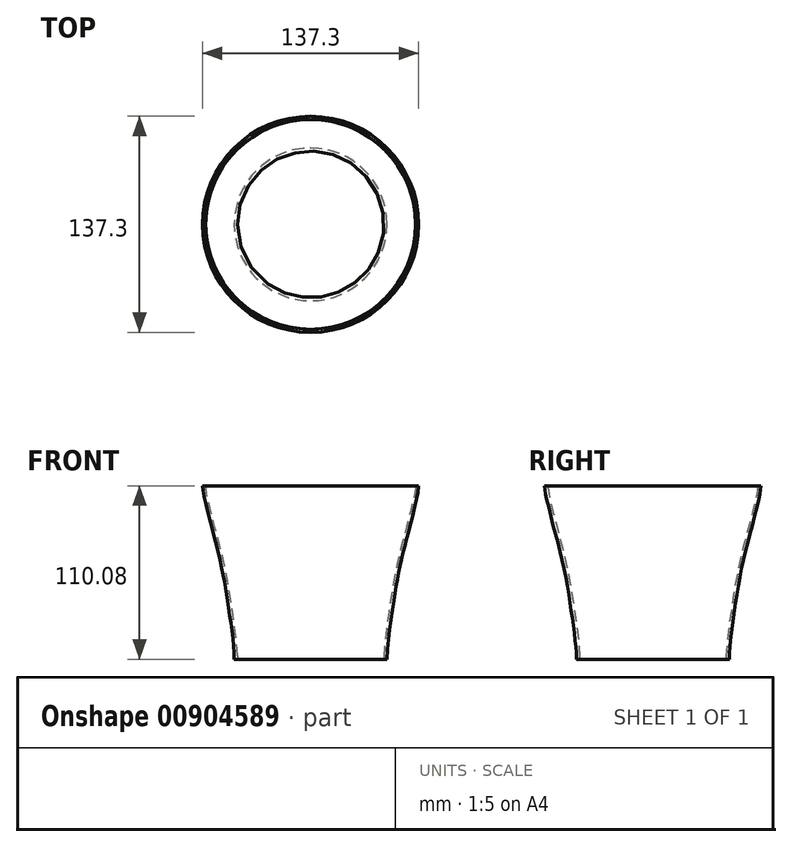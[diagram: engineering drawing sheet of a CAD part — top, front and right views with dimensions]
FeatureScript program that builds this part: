
annotation { "Feature Type Name" : "Feature", "Feature Type Description" : "" }
export const myFeature = defineFeature(function(context is Context, id is Id, definition is map)
    precondition{}
    {
        {
            var Q0;
            Q0=qCreatedBy(makeId("Front.planeOp"),FACE);
            var sketch = newSketch(context, id + "F0", { "sketchPlane" : qUnion([Q0])});
            skFitSpline(sketch, "E0", {"points": [v(-48.52, 0) * mm, v(-52.42, 34.55) * mm, v(-58.26, 65.75) * mm, v(-68.65, 110.08) * mm], "startDerivative": vector(0, 87.27) * mm, "endDerivative": vector(0, 50.37) * mm});
            skFitSpline(sketch, "E1.0", {"points": [v(-46.52, 0) * mm, v(-46.52, 1.88) * mm, v(-46.7, 5.96) * mm, v(-47.33, 12.74) * mm, v(-48.23, 19.89) * mm, v(-49.08, 25.86) * mm, v(-49.78, 30.48) * mm, v(-50.29, 33.83) * mm, v(-50.77, 37) * mm, v(-51.39, 41.06) * mm, v(-52.15, 45.92) * mm, v(-53.17, 51.81) * mm, v(-54.22, 57.08) * mm, v(-55.25, 61.72) * mm, v(-56.12, 65.44) * mm, v(-57.12, 69.48) * mm, v(-58.57, 75.18) * mm, v(-60.54, 82.68) * mm, v(-62.87, 91.6) * mm, v(-64.55, 98.37) * mm, v(-65.6, 103.04) * mm, v(-66.19, 106.07) * mm, v(-66.5, 108.11) * mm, v(-66.63, 109.38) * mm, v(-66.65, 109.88) * mm, v(-66.65, 110.08) * mm]});
            skLineSegment(sketch, "E2", {"start": v(-48.52, 0) * mm, "end": v(-46.52, 0) * mm});
            skLineSegment(sketch, "E3", {"start": v(-68.65, 110.08) * mm, "end": v(-66.65, 110.08) * mm});
            skLineSegment(sketch, "E4.bottom", {"start": v(-48.52, 0) * mm, "end": v(0, 0) * mm});
            skLineSegment(sketch, "E4.top", {"start": v(-46.55, 2) * mm, "end": v(0, 2) * mm});
            skLineSegment(sketch, "E4.left", {"start": v(-48.52, 0) * mm, "end": v(-48.52, 2) * mm});
            skLineSegment(sketch, "E4.right", {"start": v(0, 0) * mm, "end": v(0, 2) * mm});
            skSolve(sketch);
        }
        {
            var Q0;
            Q0=qCreatedBy(makeId("Top.planeOp"),FACE);
            var sketch = newSketch(context, id + "F1", { "sketchPlane" : qUnion([Q0])});
            skCircle(sketch, "E5", {"center": v(0, 0) * mm, "radius": 48.52 * mm});
            skSolve(sketch);
        }
        {
            var Q0;
            {var subQ4=sQuery(id+"F0.wireOp",EDGE,"E0");Q0=makeQuery(id+"F0.imprint","IMPRINT",FACE,{"disambiguationData":[TD([[makeQuery(id+"F0.imprint","IMPRINT",EDGE,{"derivedFrom":subQ4}),-1.0]])]});}
            var Q1;
            Q1=sQuery(id+"F1.wireOp",EDGE,"E5");
            sweep(context, id + "F2", {"profiles" : qUnion([Q0]), "path" : qUnion([Q1])});
        }
    });
